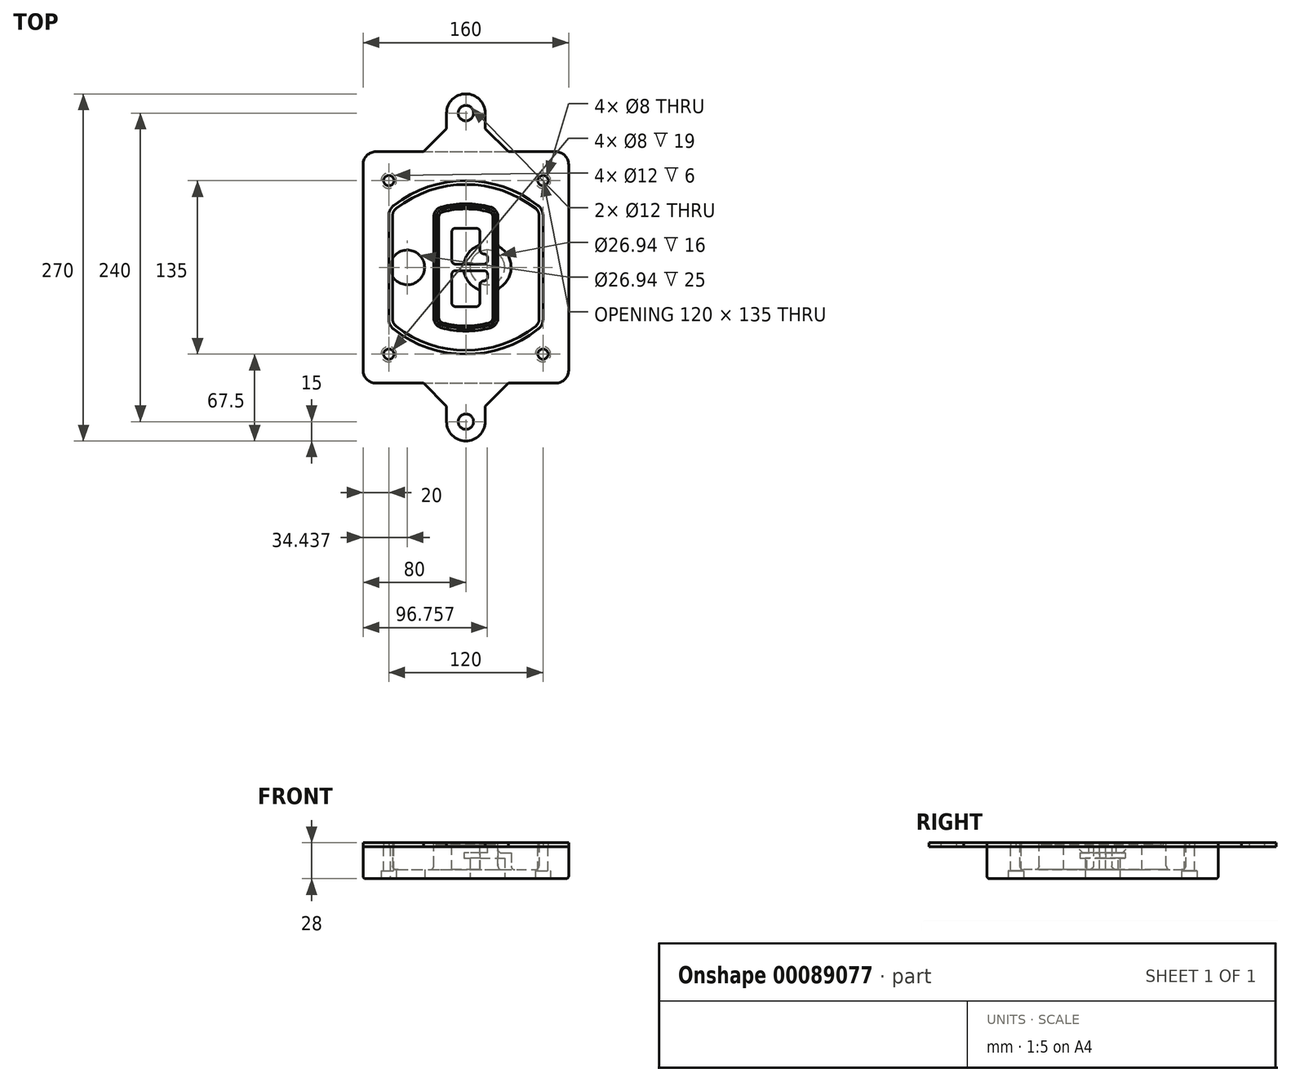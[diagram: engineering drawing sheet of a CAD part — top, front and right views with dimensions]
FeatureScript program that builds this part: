
annotation { "Feature Type Name" : "Feature", "Feature Type Description" : "" }
export const myFeature = defineFeature(function(context is Context, id is Id, definition is map)
    precondition{}
    {
        {
            var Q0;
            Q0=qCreatedBy(makeId("Top.planeOp"),FACE);
            var sketch = newSketch(context, id + "F0", { "sketchPlane" : qUnion([Q0])});
            skPoint(sketch, "E0.rect.middle", {"position": v(0, 0) * mm});
            skLineSegment(sketch, "E1.bottom", {"start": v(-70, -90) * mm, "end": v(70, -90) * mm});
            skLineSegment(sketch, "E1.top", {"start": v(-70, 90) * mm, "end": v(70, 90) * mm});
            skLineSegment(sketch, "E1.left", {"start": v(-80, -80) * mm, "end": v(-80, 80) * mm});
            skLineSegment(sketch, "E1.right", {"start": v(80, -80) * mm, "end": v(80, 80) * mm});
            skLineSegment(sketch, "E2", {"start": v(-80, 90) * mm, "end": v(80, -90) * mm, "construction": true});
            skLineSegment(sketch, "E3", {"start": v(80, 90) * mm, "end": v(-80, -90) * mm, "construction": true});
            skCircle(sketch, "E4", {"center": v(-60, 67.5) * mm, "radius": 4 * mm});
            skCircle(sketch, "E5", {"center": v(60, 67.5) * mm, "radius": 4 * mm});
            skCircle(sketch, "E6", {"center": v(60, -67.5) * mm, "radius": 4 * mm});
            skCircle(sketch, "E7", {"center": v(-60, -67.5) * mm, "radius": 4 * mm});
            skLineSegment(sketch, "E8", {"start": v(-60, 67.5) * mm, "end": v(60, 67.5) * mm, "construction": true});
            skLineSegment(sketch, "E9", {"start": v(60, 67.5) * mm, "end": v(60, -67.5) * mm, "construction": true});
            skLineSegment(sketch, "E10", {"start": v(60, -67.5) * mm, "end": v(-60, -67.5) * mm, "construction": true});
            skLineSegment(sketch, "E11", {"start": v(-60, -67.5) * mm, "end": v(-60, 67.5) * mm, "construction": true});
            skLineSegment(sketch, "E12", {"start": v(-60, 40.3) * mm, "end": v(-60, -40.3) * mm});
            skLineSegment(sketch, "E13", {"start": v(60, 40.3) * mm, "end": v(60, -40.3) * mm});
            skArc(sketch, "E14", {"start": v(56.15, 48.18) * mm, "mid": v(0, 67.5) * mm, "end": v(-56.15, 48.18) * mm});
            skArc(sketch, "E15", {"start": v(-56.15, -48.18) * mm, "mid": v(0, -67.5) * mm, "end": v(56.15, -48.18) * mm});
            skLineSegment(sketch, "E16", {"start": v(-60, 0) * mm, "end": v(60, 0) * mm, "construction": true});
            skPoint(sketch, "E17.visualSharp", {"position": v(-60, -45) * mm});
            skArc(sketch, "E17.filletArc", {"start": v(-60, -40.3) * mm, "mid": v(-58.99, -44.68) * mm, "end": v(-56.15, -48.18) * mm});
            skPoint(sketch, "E18.visualSharp", {"position": v(-60, 45) * mm});
            skArc(sketch, "E18.filletArc", {"start": v(-56.15, 48.18) * mm, "mid": v(-58.99, 44.68) * mm, "end": v(-60, 40.3) * mm});
            skPoint(sketch, "E19.visualSharp", {"position": v(60, 45) * mm});
            skArc(sketch, "E19.filletArc", {"start": v(60, 40.3) * mm, "mid": v(58.99, 44.68) * mm, "end": v(56.15, 48.18) * mm});
            skPoint(sketch, "E20.visualSharp", {"position": v(60, -45) * mm});
            skArc(sketch, "E20.filletArc", {"start": v(56.15, -48.18) * mm, "mid": v(58.99, -44.68) * mm, "end": v(60, -40.3) * mm});
            skPoint(sketch, "E21.visualSharp", {"position": v(-80, 90) * mm});
            skArc(sketch, "E21.filletArc", {"start": v(-70, 90) * mm, "mid": v(-77.07, 87.07) * mm, "end": v(-80, 80) * mm});
            skPoint(sketch, "E22.visualSharp", {"position": v(80, 90) * mm});
            skArc(sketch, "E22.filletArc", {"start": v(80, 80) * mm, "mid": v(77.07, 87.07) * mm, "end": v(70, 90) * mm});
            skPoint(sketch, "E23.visualSharp", {"position": v(80, -90) * mm});
            skArc(sketch, "E23.filletArc", {"start": v(70, -90) * mm, "mid": v(77.07, -87.07) * mm, "end": v(80, -80) * mm});
            skPoint(sketch, "E24.visualSharp", {"position": v(-80, -90) * mm});
            skArc(sketch, "E24.filletArc", {"start": v(-80, -80) * mm, "mid": v(-77.07, -87.07) * mm, "end": v(-70, -90) * mm});
            skArc(sketch, "E25.0", {"start": v(57, 40.3) * mm, "mid": v(56.3, 43.36) * mm, "end": v(54.3, 45.81) * mm});
            skLineSegment(sketch, "E25.1", {"start": v(57, 40.3) * mm, "end": v(57, -40.3) * mm});
            skArc(sketch, "E25.2", {"start": v(54.3, -45.81) * mm, "mid": v(56.3, -43.36) * mm, "end": v(57, -40.3) * mm});
            skArc(sketch, "E25.3", {"start": v(-54.3, -45.81) * mm, "mid": v(0, -64.5) * mm, "end": v(54.3, -45.81) * mm});
            skArc(sketch, "E25.4", {"start": v(-57, -40.3) * mm, "mid": v(-56.3, -43.36) * mm, "end": v(-54.3, -45.81) * mm});
            skArc(sketch, "E25.5", {"start": v(54.3, 45.81) * mm, "mid": v(0, 64.5) * mm, "end": v(-54.3, 45.81) * mm});
            skLineSegment(sketch, "E25.6", {"start": v(-57, 40.3) * mm, "end": v(-57, -40.3) * mm});
            skArc(sketch, "E25.7", {"start": v(-54.3, 45.81) * mm, "mid": v(-56.3, 43.36) * mm, "end": v(-57, 40.3) * mm});
            skArc(sketch, "E26.0", {"start": v(-58.62, 51.33) * mm, "mid": v(-62.58, 46.43) * mm, "end": v(-64, 40.3) * mm});
            skArc(sketch, "E26.1", {"start": v(58.62, 51.33) * mm, "mid": v(0, 71.5) * mm, "end": v(-58.62, 51.33) * mm});
            skArc(sketch, "E26.2", {"start": v(64, 40.3) * mm, "mid": v(62.58, 46.43) * mm, "end": v(58.62, 51.33) * mm});
            skLineSegment(sketch, "E26.3", {"start": v(64, 40.3) * mm, "end": v(64, -40.3) * mm});
            skArc(sketch, "E26.4", {"start": v(58.62, -51.33) * mm, "mid": v(62.58, -46.43) * mm, "end": v(64, -40.3) * mm});
            skLineSegment(sketch, "E26.5", {"start": v(-64, 40.3) * mm, "end": v(-64, -40.3) * mm});
            skArc(sketch, "E26.6", {"start": v(-58.62, -51.33) * mm, "mid": v(0, -71.5) * mm, "end": v(58.62, -51.33) * mm});
            skArc(sketch, "E26.7", {"start": v(-64, -40.3) * mm, "mid": v(-62.58, -46.43) * mm, "end": v(-58.62, -51.33) * mm});
            skSolve(sketch);
        }
        {
            var Q0;
            Q0=makeQuery(id+"F0.imprint","IMPRINT",FACE,{"disambiguationData":[TD([[makeQuery(id+"F0.imprint","IMPRINT",EDGE,{"derivedFrom":sQuery(id+"F0.wireOp",EDGE,"E1.bottom")}),1.0]])]});
            var Q1;
            Q1=makeQuery(id+"F0.imprint","IMPRINT",FACE,{"disambiguationData":[TD([[makeQuery(id+"F0.imprint","IMPRINT",EDGE,{"derivedFrom":sQuery(id+"F0.wireOp",EDGE,"E12")}),1.0]])]});
            var Q2;
            Q2=makeQuery(id+"F0.imprint","IMPRINT",FACE,{"disambiguationData":[TD([[makeQuery(id+"F0.imprint","IMPRINT",EDGE,{"derivedFrom":sQuery(id+"F0.wireOp",EDGE,"E25.0")}),1.0]])]});
            var Q3;
            Q3=makeQuery(id+"F0.imprint","IMPRINT",FACE,{"disambiguationData":[TD([[makeQuery(id+"F0.imprint","IMPRINT",EDGE,{"derivedFrom":sQuery(id+"F0.wireOp",EDGE,"E12")}),-1.0]])]});
            extrude(context, id + "F1", {"entities" : qUnion([Q0, Q1, Q2, Q3]), "oppositeDirection" : true, "depth" : 25 * mm});
        }
        {
            var Q0;
            Q0=makeQuery(id+"F0.imprint","IMPRINT",FACE,{"disambiguationData":[TD([[makeQuery(id+"F0.imprint","IMPRINT",EDGE,{"derivedFrom":sQuery(id+"F0.wireOp",EDGE,"E12")}),1.0]])]});
            extrude(context, id + "F2", {"entities" : qUnion([Q0]), "operationType" : NewBodyOperationType.ADD, "depth" : 3 * mm});
        }
        {
            var Q0;
            Q0=makeQuery(id+"F0.imprint","IMPRINT",FACE,{"disambiguationData":[TD([[makeQuery(id+"F0.imprint","IMPRINT",EDGE,{"derivedFrom":sQuery(id+"F0.wireOp",EDGE,"E25.0")}),1.0]])]});
            extrude(context, id + "F3", {"entities" : qUnion([Q0]), "operationType" : NewBodyOperationType.REMOVE, "oppositeDirection" : true, "depth" : 18 * mm});
        }
        {
            var Q0;
            Q0=makeQuery(id+"F2.opExtrude","CAP_FACE",FACE,{"disambiguationData":[OSD([sQuery(id+"F0.wireOp",EDGE,"E12"),sQuery(id+"F0.wireOp",EDGE,"E13"),sQuery(id+"F0.wireOp",EDGE,"E14"),sQuery(id+"F0.wireOp",EDGE,"E15"),sQuery(id+"F0.wireOp",EDGE,"E17.filletArc"),sQuery(id+"F0.wireOp",EDGE,"E18.filletArc"),sQuery(id+"F0.wireOp",EDGE,"E19.filletArc"),sQuery(id+"F0.wireOp",EDGE,"E20.filletArc"),sQuery(id+"F0.wireOp",EDGE,"E25.0"),sQuery(id+"F0.wireOp",EDGE,"E25.1"),sQuery(id+"F0.wireOp",EDGE,"E25.2"),sQuery(id+"F0.wireOp",EDGE,"E25.3"),sQuery(id+"F0.wireOp",EDGE,"E25.4"),sQuery(id+"F0.wireOp",EDGE,"E25.5"),sQuery(id+"F0.wireOp",EDGE,"E25.6"),sQuery(id+"F0.wireOp",EDGE,"E25.7")])],"isStart":false});
            var sketch = newSketch(context, id + "F4", { "sketchPlane" : qUnion([Q0])});
            skArc(sketch, "E27.0", {"start": v(-19.08, -46.97) * mm, "mid": v(0, -49.5) * mm, "end": v(19.08, -46.97) * mm});
            skArc(sketch, "E28.0", {"start": v(19.08, 46.97) * mm, "mid": v(0, 49.5) * mm, "end": v(-19.08, 46.97) * mm});
            skLineSegment(sketch, "E29", {"start": v(-25, 39.25) * mm, "end": v(-25, -39.25) * mm});
            skLineSegment(sketch, "E30", {"start": v(25, 39.25) * mm, "end": v(25, -39.25) * mm});
            skLineSegment(sketch, "E31", {"start": v(-25, 45.1) * mm, "end": v(25, 45.1) * mm, "construction": true});
            skLineSegment(sketch, "E32", {"start": v(-25, -45.1) * mm, "end": v(25, -45.1) * mm, "construction": true});
            skPoint(sketch, "E33.visualSharp", {"position": v(-25, 45.1) * mm});
            skArc(sketch, "E33.filletArc", {"start": v(-19.08, 46.97) * mm, "mid": v(-23.35, 44.11) * mm, "end": v(-25, 39.25) * mm});
            skPoint(sketch, "E34.visualSharp", {"position": v(25, 45.1) * mm});
            skArc(sketch, "E34.filletArc", {"start": v(25, 39.25) * mm, "mid": v(23.35, 44.11) * mm, "end": v(19.08, 46.97) * mm});
            skPoint(sketch, "E35.visualSharp", {"position": v(25, -45.1) * mm});
            skArc(sketch, "E35.filletArc", {"start": v(19.08, -46.97) * mm, "mid": v(23.35, -44.11) * mm, "end": v(25, -39.25) * mm});
            skPoint(sketch, "E36.visualSharp", {"position": v(-25, -45.1) * mm});
            skArc(sketch, "E36.filletArc", {"start": v(-25, -39.25) * mm, "mid": v(-23.35, -44.11) * mm, "end": v(-19.08, -46.97) * mm});
            skArc(sketch, "E37.0", {"start": v(54.3, 45.81) * mm, "mid": v(0, 64.5) * mm, "end": v(-54.3, 45.81) * mm});
            skArc(sketch, "E37.1", {"start": v(-54.3, 45.81) * mm, "mid": v(-56.3, 43.36) * mm, "end": v(-57, 40.3) * mm});
            skLineSegment(sketch, "E37.2", {"start": v(-57, 40.3) * mm, "end": v(-57, -40.3) * mm});
            skArc(sketch, "E37.3", {"start": v(-57, -40.3) * mm, "mid": v(-56.3, -43.36) * mm, "end": v(-54.3, -45.81) * mm});
            skArc(sketch, "E37.4", {"start": v(-54.3, -45.81) * mm, "mid": v(0, -64.5) * mm, "end": v(54.3, -45.81) * mm});
            skArc(sketch, "E37.5", {"start": v(54.3, -45.81) * mm, "mid": v(56.3, -43.36) * mm, "end": v(57, -40.3) * mm});
            skLineSegment(sketch, "E37.6", {"start": v(57, 40.3) * mm, "end": v(57, -40.3) * mm});
            skArc(sketch, "E37.7", {"start": v(57, 40.3) * mm, "mid": v(56.3, 43.36) * mm, "end": v(54.3, 45.81) * mm});
            skLineSegment(sketch, "E38.0", {"start": v(23, 39.25) * mm, "end": v(23, -39.25) * mm});
            skArc(sketch, "E38.1", {"start": v(18.56, -45.04) * mm, "mid": v(21.76, -42.9) * mm, "end": v(23, -39.25) * mm});
            skArc(sketch, "E38.2", {"start": v(-18.56, -45.04) * mm, "mid": v(0, -47.5) * mm, "end": v(18.56, -45.04) * mm});
            skArc(sketch, "E38.3", {"start": v(-23, -39.25) * mm, "mid": v(-21.76, -42.9) * mm, "end": v(-18.56, -45.04) * mm});
            skLineSegment(sketch, "E38.4", {"start": v(-23, 39.25) * mm, "end": v(-23, -39.25) * mm});
            skArc(sketch, "E38.5", {"start": v(23, 39.25) * mm, "mid": v(21.76, 42.9) * mm, "end": v(18.56, 45.04) * mm});
            skArc(sketch, "E38.6", {"start": v(-18.56, 45.04) * mm, "mid": v(-21.76, 42.9) * mm, "end": v(-23, 39.25) * mm});
            skArc(sketch, "E38.7", {"start": v(18.56, 45.04) * mm, "mid": v(0, 47.5) * mm, "end": v(-18.56, 45.04) * mm});
            skArc(sketch, "E39.0", {"start": v(21, 39.25) * mm, "mid": v(20.18, 41.68) * mm, "end": v(18.04, 43.1) * mm});
            skLineSegment(sketch, "E39.1", {"start": v(21, 39.25) * mm, "end": v(21, -39.25) * mm});
            skArc(sketch, "E39.2", {"start": v(18.04, -43.1) * mm, "mid": v(20.18, -41.68) * mm, "end": v(21, -39.25) * mm});
            skArc(sketch, "E39.3", {"start": v(-18.04, -43.1) * mm, "mid": v(0, -45.5) * mm, "end": v(18.04, -43.1) * mm});
            skArc(sketch, "E39.4", {"start": v(-21, -39.25) * mm, "mid": v(-20.18, -41.68) * mm, "end": v(-18.04, -43.1) * mm});
            skArc(sketch, "E39.5", {"start": v(18.04, 43.1) * mm, "mid": v(0, 45.5) * mm, "end": v(-18.04, 43.1) * mm});
            skLineSegment(sketch, "E39.6", {"start": v(-21, 39.25) * mm, "end": v(-21, -39.25) * mm});
            skArc(sketch, "E39.7", {"start": v(-18.04, 43.1) * mm, "mid": v(-20.18, 41.68) * mm, "end": v(-21, 39.25) * mm});
            skLineSegment(sketch, "E40", {"start": v(-25, 0) * mm, "end": v(25, 0) * mm, "construction": true});
            skLineSegment(sketch, "E41", {"start": v(-11, 5.5) * mm, "end": v(-11, 27.5) * mm});
            skLineSegment(sketch, "E42", {"start": v(-8, 30.5) * mm, "end": v(8, 30.5) * mm});
            skLineSegment(sketch, "E43", {"start": v(11, 27.5) * mm, "end": v(11, 13.5) * mm});
            skLineSegment(sketch, "E44", {"start": v(14, 10.5) * mm, "end": v(14, 10.5) * mm});
            skLineSegment(sketch, "E45", {"start": v(17, 7.5) * mm, "end": v(17, 5.5) * mm});
            skLineSegment(sketch, "E46", {"start": v(14, 2.5) * mm, "end": v(-8, 2.5) * mm});
            skPoint(sketch, "E47.visualSharp", {"position": v(-11, 30.5) * mm});
            skArc(sketch, "E47.filletArc", {"start": v(-8, 30.5) * mm, "mid": v(-10.12, 29.62) * mm, "end": v(-11, 27.5) * mm});
            skPoint(sketch, "E48.visualSharp", {"position": v(11, 30.5) * mm});
            skArc(sketch, "E48.filletArc", {"start": v(11, 27.5) * mm, "mid": v(10.12, 29.62) * mm, "end": v(8, 30.5) * mm});
            skPoint(sketch, "E49.visualSharp", {"position": v(11, 10.5) * mm});
            skArc(sketch, "E49.filletArc", {"start": v(11, 13.5) * mm, "mid": v(11.88, 11.38) * mm, "end": v(14, 10.5) * mm});
            skPoint(sketch, "E50.visualSharp", {"position": v(17, 10.5) * mm});
            skArc(sketch, "E50.filletArc", {"start": v(17, 7.5) * mm, "mid": v(16.12, 9.62) * mm, "end": v(14, 10.5) * mm});
            skPoint(sketch, "E51.visualSharp", {"position": v(17, 2.5) * mm});
            skArc(sketch, "E51.filletArc", {"start": v(14, 2.5) * mm, "mid": v(16.12, 3.38) * mm, "end": v(17, 5.5) * mm});
            skPoint(sketch, "E52.visualSharp", {"position": v(-11, 2.5) * mm});
            skArc(sketch, "E52.filletArc", {"start": v(-11, 5.5) * mm, "mid": v(-10.12, 3.38) * mm, "end": v(-8, 2.5) * mm});
            skLineSegment(sketch, "E53.0.MirrorCS", {"start": v(14, -2.5) * mm, "end": v(-8, -2.5) * mm});
            skArc(sketch, "E54.0.MirrorCS", {"start": v(-11, -5.5) * mm, "mid": v(-10.12, -3.38) * mm, "end": v(-8, -2.5) * mm});
            skLineSegment(sketch, "E55.0.MirrorCS", {"start": v(-11, -5.5) * mm, "end": v(-11, -27.5) * mm});
            skArc(sketch, "E56.0.MirrorCS", {"start": v(-8, -30.5) * mm, "mid": v(-10.12, -29.62) * mm, "end": v(-11, -27.5) * mm});
            skLineSegment(sketch, "E57.0.MirrorCS", {"start": v(-8, -30.5) * mm, "end": v(8, -30.5) * mm});
            skArc(sketch, "E58.0.MirrorCS", {"start": v(11, -27.5) * mm, "mid": v(10.12, -29.62) * mm, "end": v(8, -30.5) * mm});
            skLineSegment(sketch, "E59.0.MirrorCS", {"start": v(11, -27.5) * mm, "end": v(11, -13.5) * mm});
            skArc(sketch, "E60.0.MirrorCS", {"start": v(11, -13.5) * mm, "mid": v(11.88, -11.38) * mm, "end": v(14, -10.5) * mm});
            skArc(sketch, "E61.0.MirrorCS", {"start": v(17, -7.5) * mm, "mid": v(16.12, -9.62) * mm, "end": v(14, -10.5) * mm});
            skLineSegment(sketch, "E62.0.MirrorCS", {"start": v(17, -7.5) * mm, "end": v(17, -5.5) * mm});
            skArc(sketch, "E63.0.MirrorCS", {"start": v(14, -2.5) * mm, "mid": v(16.12, -3.38) * mm, "end": v(17, -5.5) * mm});
            skSolve(sketch);
        }
        {
            var Q0;
            Q0=makeQuery(id+"F4.imprint","IMPRINT",FACE,{"disambiguationData":[TD([[makeQuery(id+"F4.imprint","IMPRINT",EDGE,{"derivedFrom":sQuery(id+"F4.wireOp",EDGE,"E27.0")}),1.0]])]});
            var Q1;
            Q1=makeQuery(id+"F4.imprint","IMPRINT",FACE,{"disambiguationData":[TD([[makeQuery(id+"F4.imprint","IMPRINT",EDGE,{"derivedFrom":sQuery(id+"F4.wireOp",EDGE,"E38.0")}),-1.0]])]});
            var Q2;
            Q2=makeQuery(id+"F4.imprint","IMPRINT",FACE,{"disambiguationData":[TD([[makeQuery(id+"F4.imprint","IMPRINT",EDGE,{"derivedFrom":sQuery(id+"F4.wireOp",EDGE,"E39.0")}),1.0]])]});
            extrude(context, id + "F5", {"entities" : qUnion([Q0, Q1, Q2]), "operationType" : NewBodyOperationType.ADD, "endBound" : BoundingType.UP_TO_NEXT, "oppositeDirection" : true, "depth" : 25 * mm});
        }
        {
            var Q0;
            Q0=makeQuery(id+"F4.imprint","IMPRINT",FACE,{"disambiguationData":[TD([[makeQuery(id+"F4.imprint","IMPRINT",EDGE,{"derivedFrom":sQuery(id+"F4.wireOp",EDGE,"E38.0")}),-1.0]])]});
            extrude(context, id + "F6", {"entities" : qUnion([Q0]), "operationType" : NewBodyOperationType.REMOVE, "oppositeDirection" : true, "depth" : 2 * mm});
        }
        {
            var Q0;
            Q0=makeQuery(id+"F1.opExtrude","CAP_FACE",FACE,{"disambiguationData":[OSD([sQuery(id+"F0.wireOp",EDGE,"E1.bottom"),sQuery(id+"F0.wireOp",EDGE,"E1.top"),sQuery(id+"F0.wireOp",EDGE,"E1.left"),sQuery(id+"F0.wireOp",EDGE,"E1.right"),sQuery(id+"F0.wireOp",EDGE,"E4"),sQuery(id+"F0.wireOp",EDGE,"E5"),sQuery(id+"F0.wireOp",EDGE,"E6"),sQuery(id+"F0.wireOp",EDGE,"E7"),sQuery(id+"F0.wireOp",EDGE,"E21.filletArc"),sQuery(id+"F0.wireOp",EDGE,"E22.filletArc"),sQuery(id+"F0.wireOp",EDGE,"E23.filletArc"),sQuery(id+"F0.wireOp",EDGE,"E24.filletArc")])],"isStart":false});
            var sketch = newSketch(context, id + "F7", { "sketchPlane" : qUnion([Q0])});
            skCircle(sketch, "E64", {"center": v(16.76, 0) * mm, "radius": 13.47 * mm});
            skCircle(sketch, "E65", {"center": v(-45.56, 0) * mm, "radius": 13.47 * mm});
            skLineSegment(sketch, "E66", {"start": v(80, 0) * mm, "end": v(-80, 0) * mm});
            skCircle(sketch, "E67", {"center": v(16.76, 0) * mm, "radius": 18.47 * mm});
            skCircle(sketch, "E68", {"center": v(60, -67.5) * mm, "radius": 6 * mm});
            skCircle(sketch, "E69", {"center": v(-60, -67.5) * mm, "radius": 6 * mm});
            skCircle(sketch, "E70", {"center": v(-60, 67.5) * mm, "radius": 6 * mm});
            skCircle(sketch, "E71", {"center": v(60, 67.5) * mm, "radius": 6 * mm});
            skSolve(sketch);
        }
        {
            var Q0;
            {var subQ1=sQuery(id+"F7.wireOp",EDGE,"E66");var subQ4=sQuery(id+"F7.wireOp",EDGE,"E64");var subQ6=makeQuery(id+"F7.imprint","INTERSECT",VERTEX,{"disambiguationData":[OD(0.0)],"derivedFrom":[subQ4,subQ1]});Q0=makeQuery(id+"F7.imprint","IMPRINT",FACE,{"disambiguationData":[TD([[makeQuery(id+"F7.imprint","IMPRINT",EDGE,{"disambiguationData":[TD([[subQ6,-1.0]])],"derivedFrom":subQ4}),-1.0]])]});}
            var Q1;
            {var subQ0=sQuery(id+"F7.wireOp",EDGE,"E66");var subQ1=sQuery(id+"F7.wireOp",EDGE,"E64");var subQ3=makeQuery(id+"F7.imprint","INTERSECT",VERTEX,{"disambiguationData":[OD(0.0)],"derivedFrom":[subQ1,subQ0]});Q1=makeQuery(id+"F7.imprint","IMPRINT",FACE,{"disambiguationData":[TD([[makeQuery(id+"F7.imprint","IMPRINT",EDGE,{"disambiguationData":[TD([[subQ3,-1.0]])],"derivedFrom":subQ1}),1.0]])]});}
            var Q2;
            {var subQ0=sQuery(id+"F7.wireOp",EDGE,"E66");var subQ1=sQuery(id+"F7.wireOp",EDGE,"E64");var subQ3=makeQuery(id+"F7.imprint","INTERSECT",VERTEX,{"disambiguationData":[OD(0.0)],"derivedFrom":[subQ1,subQ0]});Q2=makeQuery(id+"F7.imprint","IMPRINT",FACE,{"disambiguationData":[TD([[makeQuery(id+"F7.imprint","IMPRINT",EDGE,{"disambiguationData":[TD([[subQ3,1.0]])],"derivedFrom":subQ1}),1.0]])]});}
            var Q3;
            {var subQ1=sQuery(id+"F7.wireOp",EDGE,"E66");var subQ4=sQuery(id+"F7.wireOp",EDGE,"E64");var subQ6=makeQuery(id+"F7.imprint","INTERSECT",VERTEX,{"disambiguationData":[OD(0.0)],"derivedFrom":[subQ4,subQ1]});Q3=makeQuery(id+"F7.imprint","IMPRINT",FACE,{"disambiguationData":[TD([[makeQuery(id+"F7.imprint","IMPRINT",EDGE,{"disambiguationData":[TD([[subQ6,1.0]])],"derivedFrom":subQ4}),-1.0]])]});}
            extrude(context, id + "F8", {"entities" : qUnion([Q0, Q1, Q2, Q3]), "operationType" : NewBodyOperationType.ADD, "oppositeDirection" : true, "depth" : 20 * mm});
        }
        {
            var Q0;
            {var subQ0=sQuery(id+"F7.wireOp",EDGE,"E66");var subQ1=sQuery(id+"F7.wireOp",EDGE,"E64");var subQ3=makeQuery(id+"F7.imprint","INTERSECT",VERTEX,{"disambiguationData":[OD(0.0)],"derivedFrom":[subQ1,subQ0]});Q0=makeQuery(id+"F7.imprint","IMPRINT",FACE,{"disambiguationData":[TD([[makeQuery(id+"F7.imprint","IMPRINT",EDGE,{"disambiguationData":[TD([[subQ3,-1.0]])],"derivedFrom":subQ1}),1.0]])]});}
            var Q1;
            {var subQ0=sQuery(id+"F7.wireOp",EDGE,"E66");var subQ1=sQuery(id+"F7.wireOp",EDGE,"E64");var subQ3=makeQuery(id+"F7.imprint","INTERSECT",VERTEX,{"disambiguationData":[OD(0.0)],"derivedFrom":[subQ1,subQ0]});Q1=makeQuery(id+"F7.imprint","IMPRINT",FACE,{"disambiguationData":[TD([[makeQuery(id+"F7.imprint","IMPRINT",EDGE,{"disambiguationData":[TD([[subQ3,1.0]])],"derivedFrom":subQ1}),1.0]])]});}
            extrude(context, id + "F9", {"entities" : qUnion([Q0, Q1]), "operationType" : NewBodyOperationType.REMOVE, "oppositeDirection" : true, "depth" : 16 * mm});
        }
        {
            var Q0;
            {var subQ0=sQuery(id+"F7.wireOp",EDGE,"E66");var subQ1=sQuery(id+"F7.wireOp",EDGE,"E65");var subQ3=makeQuery(id+"F7.imprint","INTERSECT",VERTEX,{"disambiguationData":[OD(0.0)],"derivedFrom":[subQ1,subQ0]});Q0=makeQuery(id+"F7.imprint","IMPRINT",FACE,{"disambiguationData":[TD([[makeQuery(id+"F7.imprint","IMPRINT",EDGE,{"disambiguationData":[TD([[subQ3,-1.0]])],"derivedFrom":subQ1}),1.0]])]});}
            var Q1;
            {var subQ0=sQuery(id+"F7.wireOp",EDGE,"E66");var subQ1=sQuery(id+"F7.wireOp",EDGE,"E65");var subQ3=makeQuery(id+"F7.imprint","INTERSECT",VERTEX,{"disambiguationData":[OD(0.0)],"derivedFrom":[subQ1,subQ0]});Q1=makeQuery(id+"F7.imprint","IMPRINT",FACE,{"disambiguationData":[TD([[makeQuery(id+"F7.imprint","IMPRINT",EDGE,{"disambiguationData":[TD([[subQ3,1.0]])],"derivedFrom":subQ1}),1.0]])]});}
            extrude(context, id + "F10", {"entities" : qUnion([Q0, Q1]), "operationType" : NewBodyOperationType.REMOVE, "oppositeDirection" : true, "depth" : 25 * mm});
        }
        {
            var Q0;
            Q0=makeQuery(id+"F7.imprint","IMPRINT",FACE,{"disambiguationData":[TD([[makeQuery(id+"F7.imprint","IMPRINT",EDGE,{"derivedFrom":sQuery(id+"F7.wireOp",EDGE,"E68")}),1.0]])]});
            var Q1;
            Q1=makeQuery(id+"F7.imprint","IMPRINT",FACE,{"disambiguationData":[TD([[makeQuery(id+"F7.imprint","IMPRINT",EDGE,{"derivedFrom":makeQuery(id+"F1.opExtrude","CAP_EDGE",EDGE,{"disambiguationData":[OSD([sQuery(id+"F0.wireOp",EDGE,"E5")])],"isStart":false})}),-1.0]])]});
            var Q2;
            Q2=makeQuery(id+"F7.imprint","IMPRINT",FACE,{"disambiguationData":[TD([[makeQuery(id+"F7.imprint","IMPRINT",EDGE,{"derivedFrom":sQuery(id+"F7.wireOp",EDGE,"E69")}),1.0]])]});
            var Q3;
            Q3=makeQuery(id+"F7.imprint","IMPRINT",FACE,{"disambiguationData":[TD([[makeQuery(id+"F7.imprint","IMPRINT",EDGE,{"derivedFrom":makeQuery(id+"F1.opExtrude","CAP_EDGE",EDGE,{"disambiguationData":[OSD([sQuery(id+"F0.wireOp",EDGE,"E4")])],"isStart":false})}),-1.0]])]});
            var Q4;
            Q4=makeQuery(id+"F7.imprint","IMPRINT",FACE,{"disambiguationData":[TD([[makeQuery(id+"F7.imprint","IMPRINT",EDGE,{"derivedFrom":sQuery(id+"F7.wireOp",EDGE,"E70")}),1.0]])]});
            var Q5;
            Q5=makeQuery(id+"F7.imprint","IMPRINT",FACE,{"disambiguationData":[TD([[makeQuery(id+"F7.imprint","IMPRINT",EDGE,{"derivedFrom":makeQuery(id+"F1.opExtrude","CAP_EDGE",EDGE,{"disambiguationData":[OSD([sQuery(id+"F0.wireOp",EDGE,"E7")])],"isStart":false})}),-1.0]])]});
            var Q6;
            Q6=makeQuery(id+"F7.imprint","IMPRINT",FACE,{"disambiguationData":[TD([[makeQuery(id+"F7.imprint","IMPRINT",EDGE,{"derivedFrom":sQuery(id+"F7.wireOp",EDGE,"E71")}),1.0]])]});
            var Q7;
            Q7=makeQuery(id+"F7.imprint","IMPRINT",FACE,{"disambiguationData":[TD([[makeQuery(id+"F7.imprint","IMPRINT",EDGE,{"derivedFrom":makeQuery(id+"F1.opExtrude","CAP_EDGE",EDGE,{"disambiguationData":[OSD([sQuery(id+"F0.wireOp",EDGE,"E6")])],"isStart":false})}),-1.0]])]});
            extrude(context, id + "F11", {"entities" : qUnion([Q0, Q1, Q2, Q3, Q4, Q5, Q6, Q7]), "operationType" : NewBodyOperationType.REMOVE, "oppositeDirection" : true, "depth" : 6 * mm});
        }
        {
            var Q0;
            Q0=makeQuery(id+"F9.boolean.opBoolean","COPY",FACE,{"derivedFrom":makeQuery(id+"F9.opExtrude","CAP_FACE",FACE,{"disambiguationData":[OSD([sQuery(id+"F7.wireOp",EDGE,"E64")])],"isStart":false})});
            var sketch = newSketch(context, id + "F12", { "sketchPlane" : qUnion([Q0])});
            skArc(sketch, "E72.0", {"start": v(11, 17.55) * mm, "mid": v(2.57, 11.82) * mm, "end": v(-1.54, 2.5) * mm});
            skArc(sketch, "E72.1", {"start": v(-1.54, -2.5) * mm, "mid": v(2.57, -11.82) * mm, "end": v(11, -17.55) * mm});
            skLineSegment(sketch, "E73", {"start": v(-1.54, -2.5) * mm, "end": v(14, -2.5) * mm});
            skLineSegment(sketch, "E74.0", {"start": v(14, 2.5) * mm, "end": v(-1.54, 2.5) * mm});
            skArc(sketch, "E74.1", {"start": v(14, 2.5) * mm, "mid": v(16.12, 3.38) * mm, "end": v(17, 5.5) * mm});
            skLineSegment(sketch, "E74.2", {"start": v(17, 7.5) * mm, "end": v(17, 5.5) * mm});
            skArc(sketch, "E74.3", {"start": v(17, 7.5) * mm, "mid": v(16.12, 9.62) * mm, "end": v(14, 10.5) * mm});
            skArc(sketch, "E74.4", {"start": v(11, 13.5) * mm, "mid": v(11.88, 11.38) * mm, "end": v(14, 10.5) * mm});
            skLineSegment(sketch, "E74.5", {"start": v(11, 17.55) * mm, "end": v(11, 13.5) * mm});
            skLineSegment(sketch, "E74.7", {"start": v(14, -2.5) * mm, "end": v(-1.54, -2.5) * mm});
            skArc(sketch, "E74.8", {"start": v(14, -2.5) * mm, "mid": v(16.12, -3.38) * mm, "end": v(17, -5.5) * mm});
            skLineSegment(sketch, "E74.9", {"start": v(17, -7.5) * mm, "end": v(17, -5.5) * mm});
            skArc(sketch, "E74.10", {"start": v(17, -7.5) * mm, "mid": v(16.12, -9.62) * mm, "end": v(14, -10.5) * mm});
            skArc(sketch, "E74.11", {"start": v(11, -13.5) * mm, "mid": v(11.88, -11.38) * mm, "end": v(14, -10.5) * mm});
            skLineSegment(sketch, "E74.12", {"start": v(11, -17.55) * mm, "end": v(11, -13.5) * mm});
            skPoint(sketch, "E75.orphan", {"position": v(11, -27.5) * mm});
            skPoint(sketch, "E76.orphan", {"position": v(-8, -2.5) * mm});
            skPoint(sketch, "E77.orphan", {"position": v(-8, 2.5) * mm});
            skPoint(sketch, "E78.orphan", {"position": v(11, 27.5) * mm});
            skSolve(sketch);
        }
        {
            var Q0;
            {var subQ7=sQuery(id+"F12.wireOp",EDGE,"E72.0");var subQ14=sQuery(id+"F12.wireOp",EDGE,"E72.1");var subQ16=sQuery(id+"F12.wireOp",EDGE,"E74.1");var subQ18=sQuery(id+"F12.wireOp",EDGE,"E74.8");Q0=qUnion([makeQuery(id+"F12.imprint","IMPRINT",FACE,{"disambiguationData":[TD([[makeQuery(id+"F12.imprint","IMPRINT",EDGE,{"derivedFrom":subQ7}),1.0]])]}),makeQuery(id+"F12.imprint","IMPRINT",FACE,{"disambiguationData":[TD([[makeQuery(id+"F12.imprint","IMPRINT",EDGE,{"derivedFrom":subQ14}),1.0]])]}),makeQuery(id+"F12.imprint","IMPRINT",FACE,{"disambiguationData":[TD([[makeQuery(id+"F12.imprint","IMPRINT",EDGE,{"derivedFrom":subQ16}),1.0]])]}),makeQuery(id+"F12.imprint","IMPRINT",FACE,{"disambiguationData":[TD([[makeQuery(id+"F12.imprint","IMPRINT",EDGE,{"derivedFrom":subQ18}),-1.0]])]})]);}
            var Q1;
            Q1=makeQuery(id+"F5.boolean.opBoolean","SPLIT",FACE,{"disambiguationData":[TD([makeQuery(id+"F5.opExtrude","SWEPT_FACE",FACE,{"disambiguationData":[OSD([sQuery(id+"F4.wireOp",EDGE,"E41")])]})])],"derivedFrom":makeQuery(id+"F3.boolean.opBoolean","COPY",FACE,{"derivedFrom":makeQuery(id+"F3.opExtrude","CAP_FACE",FACE,{"disambiguationData":[OSD([sQuery(id+"F0.wireOp",EDGE,"E25.0"),sQuery(id+"F0.wireOp",EDGE,"E25.1"),sQuery(id+"F0.wireOp",EDGE,"E25.2"),sQuery(id+"F0.wireOp",EDGE,"E25.3"),sQuery(id+"F0.wireOp",EDGE,"E25.4"),sQuery(id+"F0.wireOp",EDGE,"E25.5"),sQuery(id+"F0.wireOp",EDGE,"E25.6"),sQuery(id+"F0.wireOp",EDGE,"E25.7")])],"isStart":false})})});
            extrude(context, id + "F13", {"entities" : qUnion([Q0]), "operationType" : NewBodyOperationType.REMOVE, "endBound" : BoundingType.UP_TO_SURFACE, "endBoundEntityFace" : qUnion([Q1]), "depth" : 25 * mm});
        }
        {
            var Q0;
            Q0=makeQuery(id+"F3.boolean.opBoolean","COPY",EDGE,{"derivedFrom":makeQuery(id+"F3.opExtrude","CAP_EDGE",EDGE,{"disambiguationData":[OSD([sQuery(id+"F0.wireOp",EDGE,"E25.6")])],"isStart":false})});
            var Q1;
            Q1=makeQuery(id+"F8.boolean.opBoolean","INTERSECT",EDGE,{"derivedFrom":[makeQuery(id+"F5.opExtrude","SWEPT_FACE",FACE,{"disambiguationData":[OSD([sQuery(id+"F4.wireOp",EDGE,"E30")])]}),makeQuery(id+"F8.opExtrude","CAP_FACE",FACE,{"disambiguationData":[OSD([sQuery(id+"F7.wireOp",EDGE,"E67")])],"isStart":false})]});
            var Q2;
            Q2=makeQuery(id+"F8.boolean.opBoolean","INTERSECT",EDGE,{"disambiguationData":[OD(1.0)],"derivedFrom":[makeQuery(id+"F5.opExtrude","SWEPT_FACE",FACE,{"disambiguationData":[OSD([sQuery(id+"F4.wireOp",EDGE,"E30")])]}),makeQuery(id+"F8.opExtrude","SWEPT_FACE",FACE,{"disambiguationData":[OSD([sQuery(id+"F7.wireOp",EDGE,"E67")])]})]});
            var Q3;
            {var subQ0=sQuery(id+"F4.wireOp",EDGE,"E30");Q3=makeQuery(id+"F8.boolean.opBoolean","SPLIT",EDGE,{"disambiguationData":[TD([makeQuery(id+"F5.opExtrude","SWEPT_FACE",FACE,{"disambiguationData":[OSD([sQuery(id+"F4.wireOp",EDGE,"E35.filletArc")])]})])],"derivedFrom":makeQuery(id+"F5.opExtrude","CAP_EDGE",EDGE,{"disambiguationData":[OSD([subQ0])],"isStart":false})});}
            var Q4;
            {var subQ0=sQuery(id+"F0.wireOp",EDGE,"E25.7");var subQ1=sQuery(id+"F0.wireOp",EDGE,"E25.1");var subQ2=sQuery(id+"F0.wireOp",EDGE,"E25.6");var subQ3=sQuery(id+"F0.wireOp",EDGE,"E25.5");var subQ4=sQuery(id+"F0.wireOp",EDGE,"E25.4");var subQ5=sQuery(id+"F0.wireOp",EDGE,"E25.0");var subQ6=sQuery(id+"F0.wireOp",EDGE,"E25.2");var subQ7=sQuery(id+"F0.wireOp",EDGE,"E25.3");Q4=makeQuery(id+"F8.boolean.opBoolean","INTERSECT",EDGE,{"derivedFrom":[makeQuery(id+"F5.boolean.opBoolean","SPLIT",FACE,{"disambiguationData":[TD([makeQuery(id+"F2.opExtrude","SWEPT_FACE",FACE,{"disambiguationData":[OSD([subQ5])]})])],"derivedFrom":makeQuery(id+"F3.boolean.opBoolean","COPY",FACE,{"derivedFrom":makeQuery(id+"F3.opExtrude","CAP_FACE",FACE,{"disambiguationData":[OSD([subQ5,subQ1,subQ6,subQ7,subQ4,subQ3,subQ2,subQ0])],"isStart":false})})}),makeQuery(id+"F8.opExtrude","SWEPT_FACE",FACE,{"disambiguationData":[OSD([sQuery(id+"F7.wireOp",EDGE,"E67")])]})]});}
            var Q5;
            Q5=makeQuery(id+"F8.boolean.opBoolean","INTERSECT",EDGE,{"disambiguationData":[OD(0.0)],"derivedFrom":[makeQuery(id+"F5.opExtrude","SWEPT_FACE",FACE,{"disambiguationData":[OSD([sQuery(id+"F4.wireOp",EDGE,"E30")])]}),makeQuery(id+"F8.opExtrude","SWEPT_FACE",FACE,{"disambiguationData":[OSD([sQuery(id+"F7.wireOp",EDGE,"E67")])]})]});
            fillet(context, id + "F14", {"entities" : qUnion([Q0, Q1, Q2, Q3, Q4, Q5]), "radius" : 3 * mm, "tangentPropagation" : true, "allowEdgeOverflow" : false});
        }
        {
            var Q0;
            Q0=makeQuery(id+"F1.opExtrude","CAP_EDGE",EDGE,{"disambiguationData":[OSD([sQuery(id+"F0.wireOp",EDGE,"E1.bottom")])],"isStart":false});
            fillet(context, id + "F15", {"entities" : qUnion([Q0]), "radius" : 2 * mm, "tangentPropagation" : true, "allowEdgeOverflow" : false});
        }
        {
            var Q0;
            {var subQ0=sQuery(id+"F0.wireOp",EDGE,"E22.filletArc");var subQ1=sQuery(id+"F0.wireOp",EDGE,"E7");var subQ2=sQuery(id+"F0.wireOp",EDGE,"E6");var subQ3=sQuery(id+"F0.wireOp",EDGE,"E5");var subQ4=sQuery(id+"F0.wireOp",EDGE,"E4");var subQ5=sQuery(id+"F0.wireOp",EDGE,"E1.bottom");var subQ6=sQuery(id+"F0.wireOp",EDGE,"E21.filletArc");var subQ7=sQuery(id+"F0.wireOp",EDGE,"E1.top");var subQ8=sQuery(id+"F0.wireOp",EDGE,"E1.left");var subQ9=sQuery(id+"F0.wireOp",EDGE,"E1.right");var subQ10=sQuery(id+"F0.wireOp",EDGE,"E23.filletArc");var subQ11=sQuery(id+"F0.wireOp",EDGE,"E24.filletArc");Q0=makeQuery(id+"F2.boolean.opBoolean","SPLIT",FACE,{"disambiguationData":[TD([makeQuery(id+"F1.opExtrude","SWEPT_FACE",FACE,{"disambiguationData":[OSD([subQ5])]})])],"derivedFrom":makeQuery(id+"F1.opExtrude","CAP_FACE",FACE,{"disambiguationData":[OSD([subQ5,subQ7,subQ8,subQ9,subQ4,subQ3,subQ2,subQ1,subQ6,subQ0,subQ10,subQ11])],"isStart":true})});}
            var sketch = newSketch(context, id + "F16", { "sketchPlane" : qUnion([Q0])});
            skLineSegment(sketch, "E79", {"start": v(-33, 90) * mm, "end": v(-15, 108) * mm});
            skLineSegment(sketch, "E80", {"start": v(-15, 108) * mm, "end": v(-15, 120) * mm});
            skArc(sketch, "E81", {"start": v(15, 120) * mm, "mid": v(0, 135) * mm, "end": v(-15, 120) * mm});
            skLineSegment(sketch, "E82", {"start": v(15, 120) * mm, "end": v(15, 108) * mm});
            skLineSegment(sketch, "E83", {"start": v(15, 108) * mm, "end": v(33, 90) * mm});
            skCircle(sketch, "E84", {"center": v(0, 120) * mm, "radius": 6 * mm});
            skLineSegment(sketch, "E85", {"start": v(0, 120) * mm, "end": v(0, 90) * mm, "construction": true});
            skLineSegment(sketch, "E86", {"start": v(-80, 0) * mm, "end": v(80, 0) * mm, "construction": true});
            skLineSegment(sketch, "E87.MirrorCS", {"start": v(-33, -90) * mm, "end": v(-15, -108) * mm});
            skLineSegment(sketch, "E88.MirrorCS", {"start": v(-15, -108) * mm, "end": v(-15, -120) * mm});
            skArc(sketch, "E89.MirrorCS", {"start": v(15, -120) * mm, "mid": v(0, -135) * mm, "end": v(-15, -120) * mm});
            skLineSegment(sketch, "E90.MirrorCS", {"start": v(15, -120) * mm, "end": v(15, -108) * mm});
            skLineSegment(sketch, "E91.MirrorCS", {"start": v(15, -108) * mm, "end": v(33, -90) * mm});
            skCircle(sketch, "E92.MirrorC", {"center": v(0, -120) * mm, "radius": 6 * mm});
            skLineSegment(sketch, "E93.MirrorCS", {"start": v(0, -120) * mm, "end": v(0, -90) * mm, "construction": true});
            skSolve(sketch);
        }
        {
            var Q0;
            {var subQ0=sQuery(id+"F16.wireOp",EDGE,"E79");Q0=makeQuery(id+"F16.imprint","IMPRINT",FACE,{"disambiguationData":[TD([[makeQuery(id+"F16.imprint","IMPRINT",EDGE,{"derivedFrom":subQ0}),-1.0]])]});}
            var Q1;
            Q1=makeQuery(id+"F16.imprint","IMPRINT",FACE,{"disambiguationData":[TD([[makeQuery(id+"F16.imprint","IMPRINT",EDGE,{"derivedFrom":makeQuery(id+"F1.opExtrude","CAP_EDGE",EDGE,{"disambiguationData":[OSD([sQuery(id+"F0.wireOp",EDGE,"E1.left")])],"isStart":true})}),-1.0]])]});
            var Q2;
            {var subQ0=sQuery(id+"F16.wireOp",EDGE,"E87.MirrorCS");Q2=makeQuery(id+"F16.imprint","IMPRINT",FACE,{"disambiguationData":[TD([[makeQuery(id+"F16.imprint","IMPRINT",EDGE,{"derivedFrom":subQ0}),1.0]])]});}
            extrude(context, id + "F17", {"entities" : qUnion([Q0, Q1, Q2]), "depth" : 3 * mm});
        }
    });
